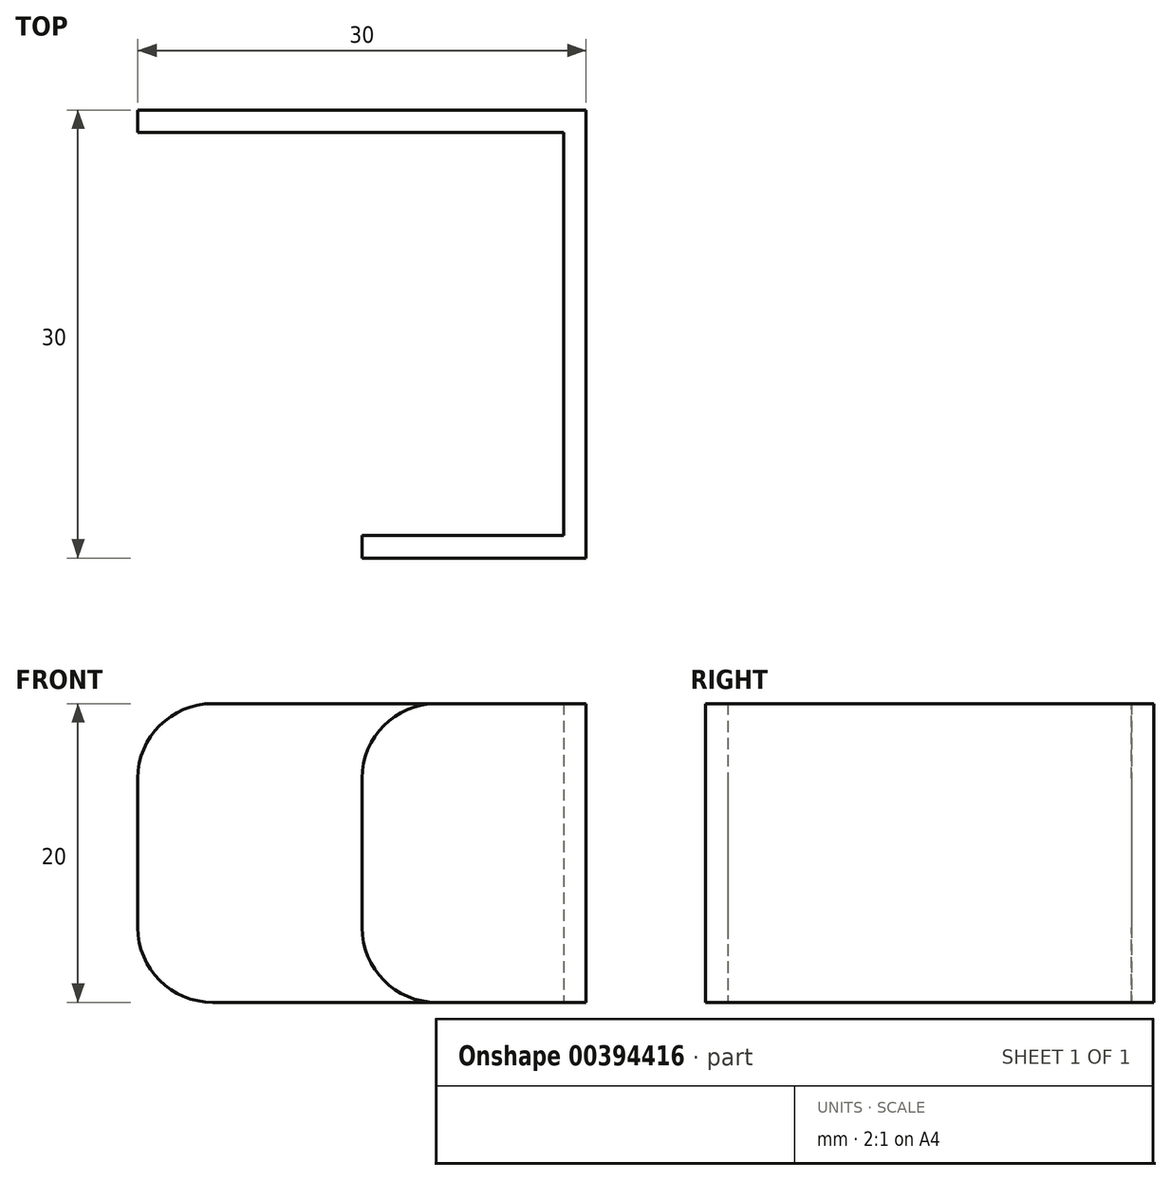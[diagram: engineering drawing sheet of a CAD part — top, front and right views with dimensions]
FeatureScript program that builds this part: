
annotation { "Feature Type Name" : "Feature", "Feature Type Description" : "" }
export const myFeature = defineFeature(function(context is Context, id is Id, definition is map)
    precondition{}
    {
        {
            var Q0;
            Q0=qCreatedBy(makeId("Top.planeOp"),FACE);
            var sketch = newSketch(context, id + "F0", { "sketchPlane" : qUnion([Q0])});
            skLineSegment(sketch, "E0", {"start": v(0, 0) * mm, "end": v(-30, 0) * mm});
            skLineSegment(sketch, "E1", {"start": v(-30, 0) * mm, "end": v(-30, -1.5) * mm});
            skLineSegment(sketch, "E2", {"start": v(-30, -1.5) * mm, "end": v(-1.5, -1.5) * mm});
            skLineSegment(sketch, "E3", {"start": v(-1.5, -1.5) * mm, "end": v(-1.5, -28.5) * mm});
            skLineSegment(sketch, "E4", {"start": v(-1.5, -28.5) * mm, "end": v(-15, -28.5) * mm});
            skLineSegment(sketch, "E5", {"start": v(-15, -28.5) * mm, "end": v(-15, -30) * mm});
            skLineSegment(sketch, "E6", {"start": v(-15, -30) * mm, "end": v(0, -30) * mm});
            skLineSegment(sketch, "E7", {"start": v(0, -30) * mm, "end": v(0, 0) * mm});
            skSolve(sketch);
        }
        {
            var Q0;
            Q0=makeQuery(id+"F0.imprint","IMPRINT",FACE,{"disambiguationData":[TD([[makeQuery(id+"F0.imprint","IMPRINT",EDGE,{"derivedFrom":sQuery(id+"F0.wireOp",EDGE,"E0")}),1.0]])]});
            extrude(context, id + "F1", {"entities" : qUnion([Q0]), "depth" : 20 * mm, "offsetDistance" : 25 * mm});
        }
        {
            var Q0;
            Q0=makeQuery(id+"F1.opExtrude","CAP_EDGE",EDGE,{"disambiguationData":[OSD([sQuery(id+"F0.wireOp",EDGE,"E1")])],"isStart":false});
            var Q1;
            Q1=makeQuery(id+"F1.opExtrude","CAP_EDGE",EDGE,{"disambiguationData":[OSD([sQuery(id+"F0.wireOp",EDGE,"E5")])],"isStart":false});
            var Q2;
            Q2=makeQuery(id+"F1.opExtrude","CAP_EDGE",EDGE,{"disambiguationData":[OSD([sQuery(id+"F0.wireOp",EDGE,"E5")])],"isStart":true});
            var Q3;
            Q3=makeQuery(id+"F1.opExtrude","CAP_EDGE",EDGE,{"disambiguationData":[OSD([sQuery(id+"F0.wireOp",EDGE,"E1")])],"isStart":true});
            fillet(context, id + "F2", {"entities" : qUnion([Q0, Q1, Q2, Q3]), "radius" : 5 * mm, "tangentPropagation" : true, "allowEdgeOverflow" : false});
        }
    });
